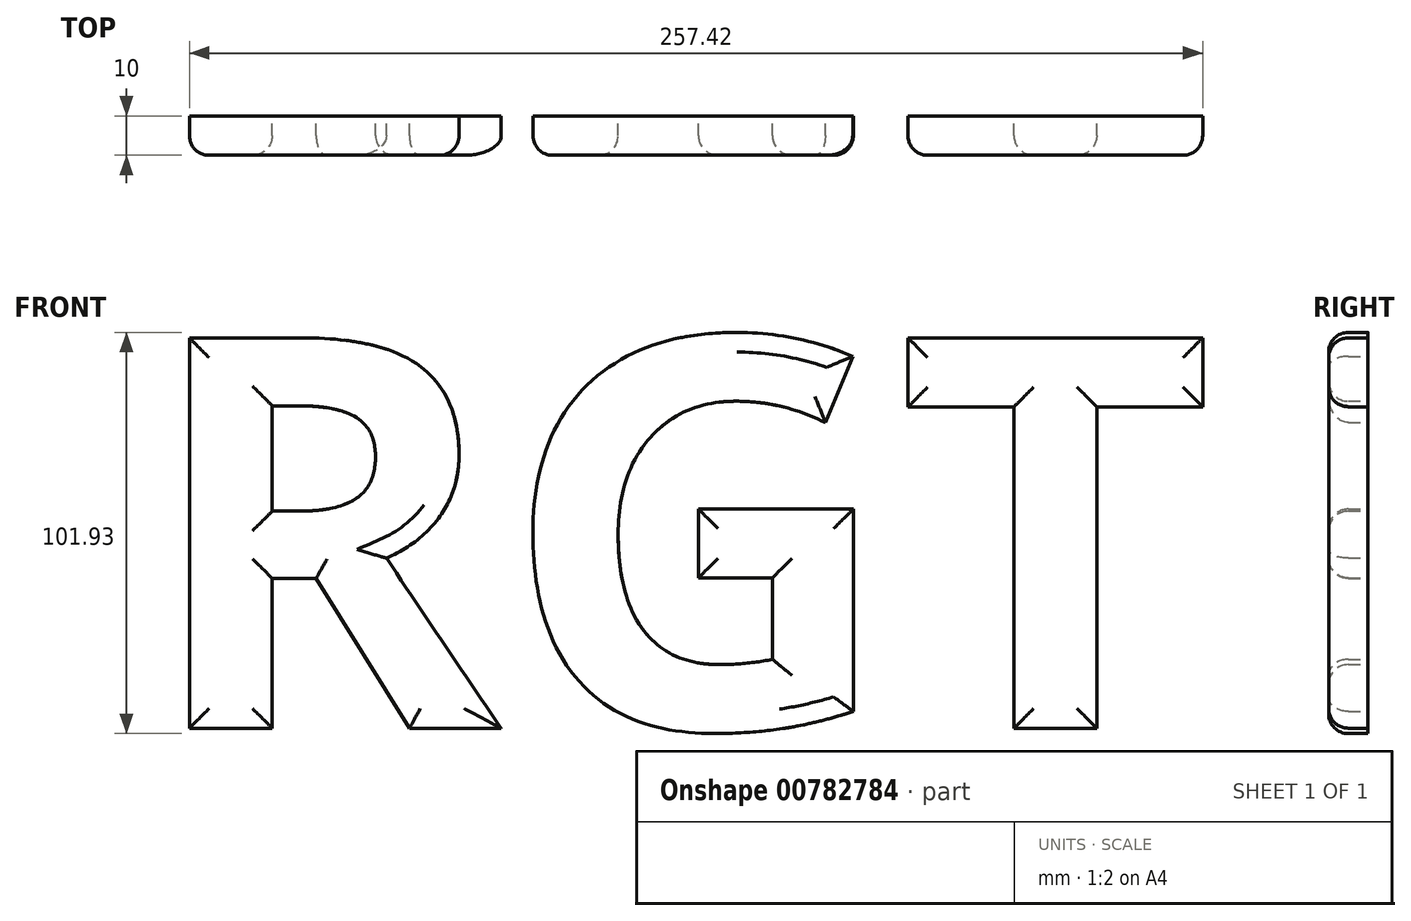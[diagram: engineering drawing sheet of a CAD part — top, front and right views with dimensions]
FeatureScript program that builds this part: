
annotation { "Feature Type Name" : "Feature", "Feature Type Description" : "" }
export const myFeature = defineFeature(function(context is Context, id is Id, definition is map)
    precondition{}
    {
        {
            var Q0;
            Q0=qCreatedBy(makeId("Front.planeOp"),FACE);
            var sketch = newSketch(context, id + "F0", { "sketchPlane" : qUnion([Q0])});
            skText(sketch, "E0", { "text": "RGT", "fontName": "OpenSans-Bold.ttf"});
            const initialGuessF0  = {"E0": [-0.0661, -0.0485, 1, 0, 0.1]};
            skSetInitialGuess(sketch, initialGuessF0);
            skSolve(sketch);
        }
        {
            var Q0;
            Q0=makeQuery(id+"F0.imprint","IMPRINT",FACE,{"disambiguationData":[TD([[makeQuery(id+"F0.imprint","IMPRINT",EDGE,{"derivedFrom":sQuery(id+"F0.wireOp",EDGE,"E0.sketch_text.stroke-0")}),-1.0]])]});
            var Q1;
            Q1=makeQuery(id+"F0.imprint","IMPRINT",FACE,{"disambiguationData":[TD([[makeQuery(id+"F0.imprint","IMPRINT",EDGE,{"derivedFrom":sQuery(id+"F0.wireOp",EDGE,"E0.sketch_text.stroke-19")}),-1.0]])]});
            var Q2;
            Q2=makeQuery(id+"F0.imprint","IMPRINT",FACE,{"disambiguationData":[TD([[makeQuery(id+"F0.imprint","IMPRINT",EDGE,{"derivedFrom":sQuery(id+"F0.wireOp",EDGE,"E0.sketch_text.stroke-38")}),-1.0]])]});
            extrude(context, id + "F1", {"entities" : qUnion([Q0, Q1, Q2]), "depth" : 10 * mm, "offsetDistance" : 25 * mm});
        }
        {
            var Q0;
            Q0=makeQuery(id+"F1.opExtrude","CAP_EDGE",EDGE,{"disambiguationData":[OSD([sQuery(id+"F0.wireOp",EDGE,"E0.sketch_text.stroke-11")])],"isStart":false});
            var Q1;
            Q1=makeQuery(id+"F1.opExtrude","CAP_EDGE",EDGE,{"disambiguationData":[OSD([sQuery(id+"F0.wireOp",EDGE,"E0.sketch_text.stroke-12")])],"isStart":false});
            var Q2;
            Q2=makeQuery(id+"F1.opExtrude","CAP_EDGE",EDGE,{"disambiguationData":[OSD([sQuery(id+"F0.wireOp",EDGE,"E0.sketch_text.stroke-15")])],"isStart":false});
            var Q3;
            Q3=makeQuery(id+"F1.opExtrude","CAP_EDGE",EDGE,{"disambiguationData":[OSD([sQuery(id+"F0.wireOp",EDGE,"E0.sketch_text.stroke-17")])],"isStart":false});
            var Q4;
            Q4=makeQuery(id+"F1.opExtrude","CAP_EDGE",EDGE,{"disambiguationData":[OSD([sQuery(id+"F0.wireOp",EDGE,"E0.sketch_text.stroke-7")])],"isStart":false});
            var Q5;
            Q5=makeQuery(id+"F1.opExtrude","CAP_EDGE",EDGE,{"disambiguationData":[OSD([sQuery(id+"F0.wireOp",EDGE,"E0.sketch_text.stroke-9")])],"isStart":false});
            var Q6;
            Q6=makeQuery(id+"F1.opExtrude","CAP_EDGE",EDGE,{"disambiguationData":[OSD([sQuery(id+"F0.wireOp",EDGE,"E0.sketch_text.stroke-18")])],"isStart":false});
            var Q7;
            Q7=makeQuery(id+"F1.opExtrude","CAP_FACE",FACE,{"disambiguationData":[OSD([sQuery(id+"F0.wireOp",EDGE,"E0.sketch_text.stroke-19"),sQuery(id+"F0.wireOp",EDGE,"E0.sketch_text.stroke-20"),sQuery(id+"F0.wireOp",EDGE,"E0.sketch_text.stroke-21"),sQuery(id+"F0.wireOp",EDGE,"E0.sketch_text.stroke-22"),sQuery(id+"F0.wireOp",EDGE,"E0.sketch_text.stroke-23"),sQuery(id+"F0.wireOp",EDGE,"E0.sketch_text.stroke-24"),sQuery(id+"F0.wireOp",EDGE,"E0.sketch_text.stroke-25"),sQuery(id+"F0.wireOp",EDGE,"E0.sketch_text.stroke-26"),sQuery(id+"F0.wireOp",EDGE,"E0.sketch_text.stroke-27"),sQuery(id+"F0.wireOp",EDGE,"E0.sketch_text.stroke-28"),sQuery(id+"F0.wireOp",EDGE,"E0.sketch_text.stroke-29"),sQuery(id+"F0.wireOp",EDGE,"E0.sketch_text.stroke-30"),sQuery(id+"F0.wireOp",EDGE,"E0.sketch_text.stroke-31"),sQuery(id+"F0.wireOp",EDGE,"E0.sketch_text.stroke-32"),sQuery(id+"F0.wireOp",EDGE,"E0.sketch_text.stroke-33"),sQuery(id+"F0.wireOp",EDGE,"E0.sketch_text.stroke-34"),sQuery(id+"F0.wireOp",EDGE,"E0.sketch_text.stroke-35"),sQuery(id+"F0.wireOp",EDGE,"E0.sketch_text.stroke-36"),sQuery(id+"F0.wireOp",EDGE,"E0.sketch_text.stroke-37")])],"isStart":false});
            var Q8;
            Q8=makeQuery(id+"F1.opExtrude","CAP_FACE",FACE,{"disambiguationData":[OSD([sQuery(id+"F0.wireOp",EDGE,"E0.sketch_text.stroke-0"),sQuery(id+"F0.wireOp",EDGE,"E0.sketch_text.stroke-1"),sQuery(id+"F0.wireOp",EDGE,"E0.sketch_text.stroke-2"),sQuery(id+"F0.wireOp",EDGE,"E0.sketch_text.stroke-3"),sQuery(id+"F0.wireOp",EDGE,"E0.sketch_text.stroke-4"),sQuery(id+"F0.wireOp",EDGE,"E0.sketch_text.stroke-5"),sQuery(id+"F0.wireOp",EDGE,"E0.sketch_text.stroke-6"),sQuery(id+"F0.wireOp",EDGE,"E0.sketch_text.stroke-7"),sQuery(id+"F0.wireOp",EDGE,"E0.sketch_text.stroke-8"),sQuery(id+"F0.wireOp",EDGE,"E0.sketch_text.stroke-9"),sQuery(id+"F0.wireOp",EDGE,"E0.sketch_text.stroke-10"),sQuery(id+"F0.wireOp",EDGE,"E0.sketch_text.stroke-11"),sQuery(id+"F0.wireOp",EDGE,"E0.sketch_text.stroke-12"),sQuery(id+"F0.wireOp",EDGE,"E0.sketch_text.stroke-13"),sQuery(id+"F0.wireOp",EDGE,"E0.sketch_text.stroke-14"),sQuery(id+"F0.wireOp",EDGE,"E0.sketch_text.stroke-15"),sQuery(id+"F0.wireOp",EDGE,"E0.sketch_text.stroke-16"),sQuery(id+"F0.wireOp",EDGE,"E0.sketch_text.stroke-17"),sQuery(id+"F0.wireOp",EDGE,"E0.sketch_text.stroke-18")])],"isStart":false});
            var Q9;
            Q9=makeQuery(id+"F1.opExtrude","CAP_FACE",FACE,{"disambiguationData":[OSD([sQuery(id+"F0.wireOp",EDGE,"E0.sketch_text.stroke-38"),sQuery(id+"F0.wireOp",EDGE,"E0.sketch_text.stroke-39"),sQuery(id+"F0.wireOp",EDGE,"E0.sketch_text.stroke-40"),sQuery(id+"F0.wireOp",EDGE,"E0.sketch_text.stroke-41"),sQuery(id+"F0.wireOp",EDGE,"E0.sketch_text.stroke-42"),sQuery(id+"F0.wireOp",EDGE,"E0.sketch_text.stroke-43"),sQuery(id+"F0.wireOp",EDGE,"E0.sketch_text.stroke-44"),sQuery(id+"F0.wireOp",EDGE,"E0.sketch_text.stroke-45")])],"isStart":false});
            fillet(context, id + "F2", {"entities" : qUnion([Q0, Q1, Q2, Q3, Q4, Q5, Q6, Q7, Q8, Q9]), "radius" : 5 * mm, "tangentPropagation" : true, "allowEdgeOverflow" : false});
        }
    });
